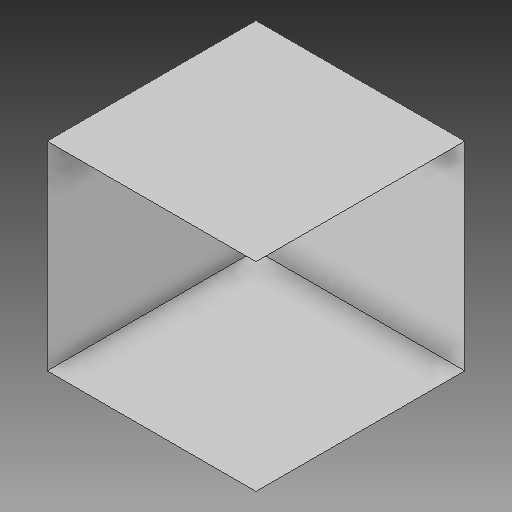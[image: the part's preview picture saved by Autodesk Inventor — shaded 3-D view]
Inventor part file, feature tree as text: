
AUTODESK INVENTOR PART (.ipt)
format: ipt  version: 2017 (Build 210142000, 142)  size: 98,816 bytes
history: native  units: in
note: dims shown in document units (in); Inventor stores cm internally (conversion verified against a paired STEP export)
features: extrude x1, other x1, sketch x1
ambient origin geometry x8: Origin, YZ Plane, XZ Plane, XY Plane, X Axis, Y Axis, Z Axis, Center Point
bodies: Solid1 (feature_tree)
feature tree (3):
  extrude  "corridor"  Depth=6.6667in
  other  "removed ends"
  sketch  "Sketch1"  dims[d0=6.6667in d1=7.0in d2=7.0in d3=0.0in]
